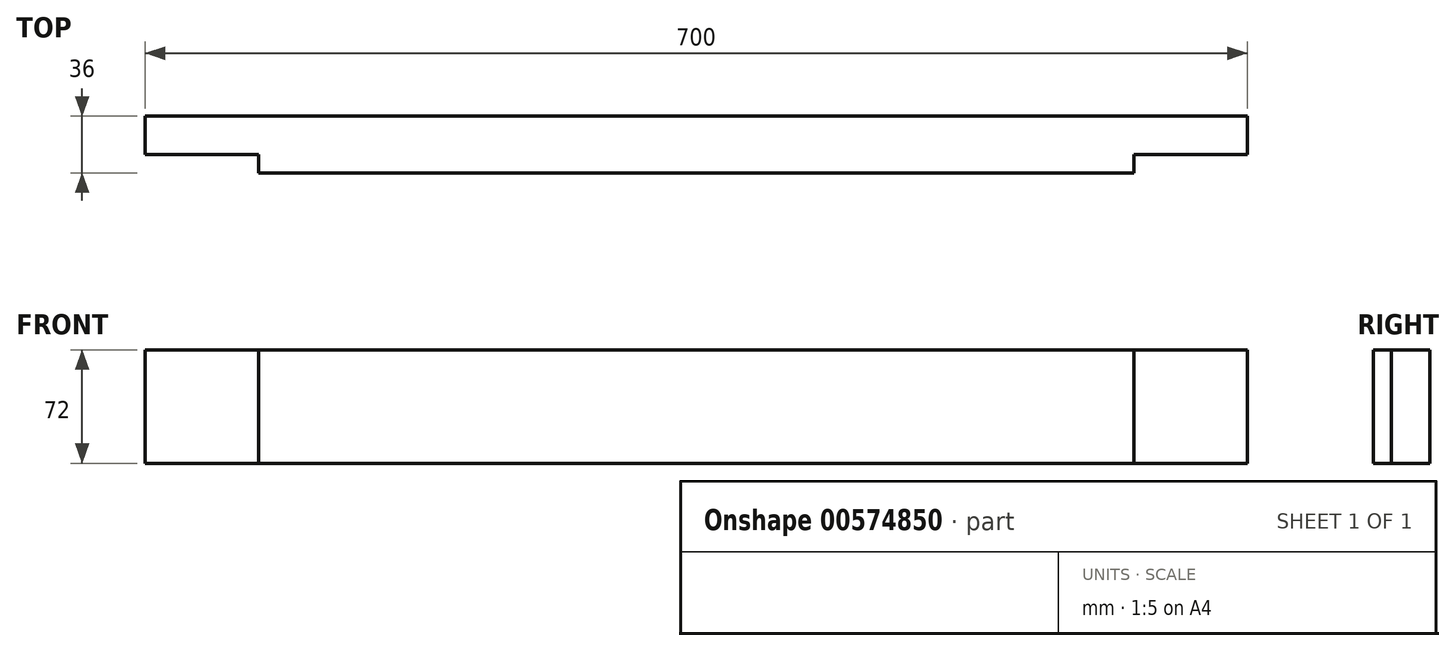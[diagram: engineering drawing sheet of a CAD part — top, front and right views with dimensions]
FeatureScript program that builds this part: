
annotation { "Feature Type Name" : "Feature", "Feature Type Description" : "" }
export const myFeature = defineFeature(function(context is Context, id is Id, definition is map)
    precondition{}
    {
        {
            var Q0;
            Q0=qCreatedBy(makeId("Front.planeOp"),FACE);
            var sketch = newSketch(context, id + "F0", { "sketchPlane" : qUnion([Q0])});
            skLineSegment(sketch, "E0.bottom", {"start": v(-350, -36) * mm, "end": v(350, -36) * mm});
            skLineSegment(sketch, "E0.top", {"start": v(-350, 36) * mm, "end": v(350, 36) * mm});
            skLineSegment(sketch, "E0.left", {"start": v(-350, -36) * mm, "end": v(-350, 36) * mm});
            skLineSegment(sketch, "E0.right", {"start": v(350, -36) * mm, "end": v(350, 36) * mm});
            skPoint(sketch, "E0.middle", {"position": v(0, 0) * mm});
            skSolve(sketch);
        }
        {
            var Q0;
            Q0=makeQuery(id+"F0.imprint","IMPRINT",FACE,{"disambiguationData":[TD([[makeQuery(id+"F0.imprint","IMPRINT",EDGE,{"derivedFrom":sQuery(id+"F0.wireOp",EDGE,"E0.bottom")}),1.0]])]});
            extrude(context, id + "F1", {"entities" : qUnion([Q0]), "endBound" : BoundingType.SYMMETRIC, "depth" : 36 * mm, "offsetDistance" : 25 * mm});
        }
        {
            var Q0;
            Q0=makeQuery(id+"F1.opExtrude","CAP_FACE",FACE,{"disambiguationData":[OSD([sQuery(id+"F0.wireOp",EDGE,"E0.bottom"),sQuery(id+"F0.wireOp",EDGE,"E0.top"),sQuery(id+"F0.wireOp",EDGE,"E0.left"),sQuery(id+"F0.wireOp",EDGE,"E0.right")])],"isStart":false});
            var sketch = newSketch(context, id + "F2", { "sketchPlane" : qUnion([Q0])});
            skLineSegment(sketch, "E1.bottom", {"start": v(-350, 36) * mm, "end": v(-278, 36) * mm});
            skLineSegment(sketch, "E1.top", {"start": v(-350, -36) * mm, "end": v(-278, -36) * mm});
            skLineSegment(sketch, "E1.left", {"start": v(-350, 36) * mm, "end": v(-350, -36) * mm});
            skLineSegment(sketch, "E1.right", {"start": v(-278, 36) * mm, "end": v(-278, -36) * mm});
            skLineSegment(sketch, "E2.bottom", {"start": v(350, 36) * mm, "end": v(278, 36) * mm});
            skLineSegment(sketch, "E2.top", {"start": v(350, -36) * mm, "end": v(278, -36) * mm});
            skLineSegment(sketch, "E2.left", {"start": v(350, 36) * mm, "end": v(350, -36) * mm});
            skLineSegment(sketch, "E2.right", {"start": v(278, 36) * mm, "end": v(278, -36) * mm});
            skSolve(sketch);
        }
        {
            var Q0;
            Q0 = qSketchRegion(id + "F2", true);
            extrude(context, id + "F3", {"entities" : qUnion([Q0]), "operationType" : NewBodyOperationType.REMOVE, "oppositeDirection" : true, "depth" : 11.65 * mm, "offsetDistance" : 25 * mm});
        }
    });
